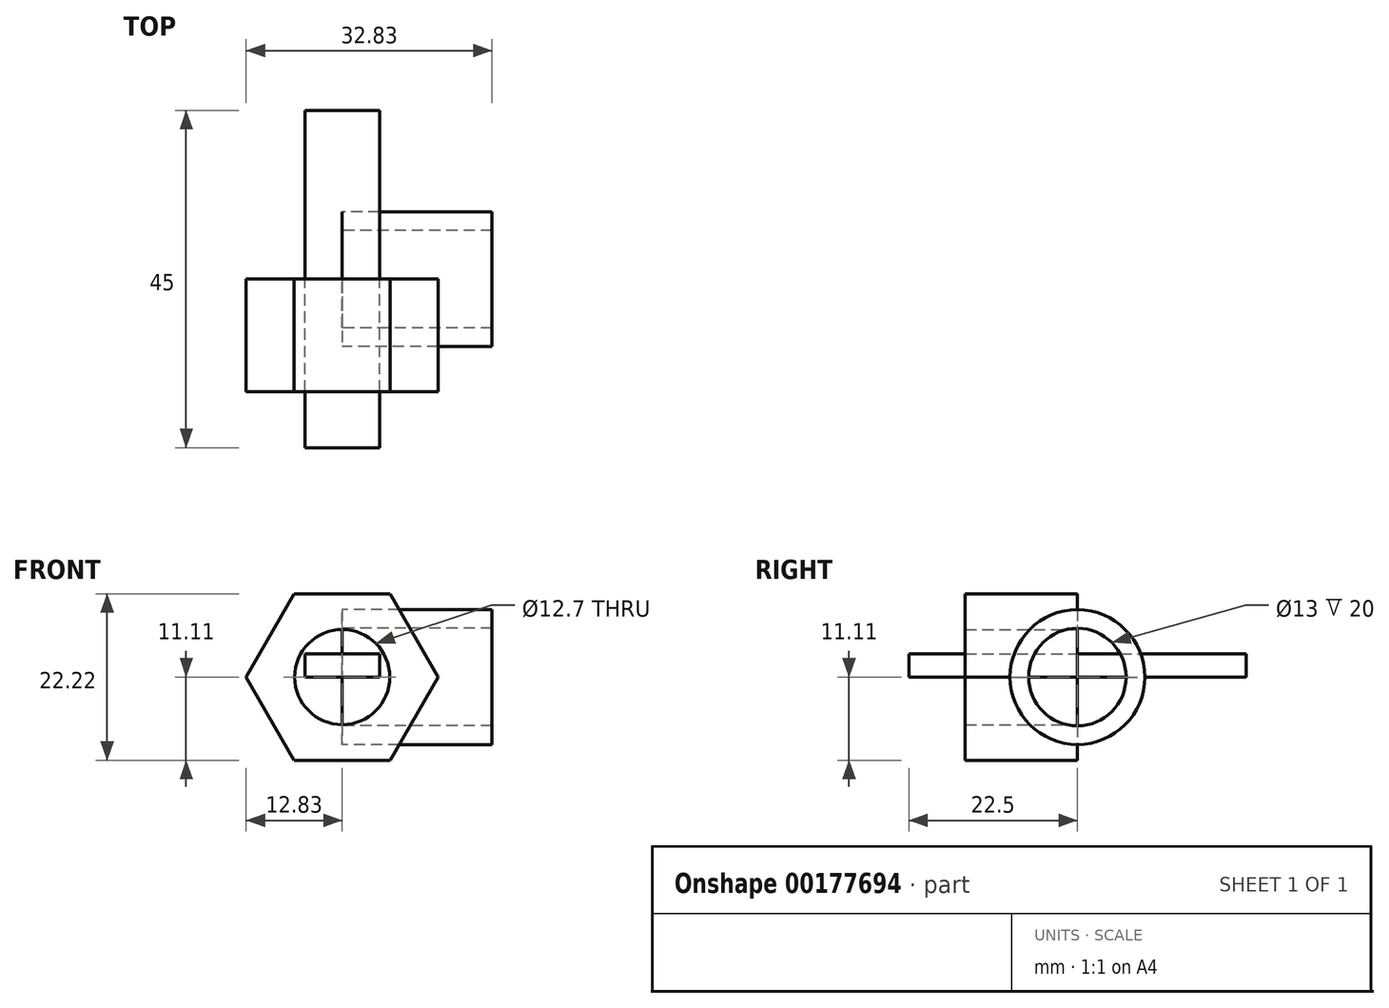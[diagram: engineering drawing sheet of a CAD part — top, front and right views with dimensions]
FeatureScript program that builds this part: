
annotation { "Feature Type Name" : "Feature", "Feature Type Description" : "" }
export const myFeature = defineFeature(function(context is Context, id is Id, definition is map)
    precondition{}
    {
        {
            var Q0;
            Q0=qCreatedBy(makeId("Front.planeOp"),FACE);
            var sketch = newSketch(context, id + "F0", { "sketchPlane" : qUnion([Q0])});
            skCircle(sketch, "E0.cCircle", {"center": v(0, 0) * mm, "radius": 11.11 * mm, "construction": true});
            skLineSegment(sketch, "E0.0", {"start": v(-6.42, 11.11) * mm, "end": v(6.42, 11.11) * mm});
            skLineSegment(sketch, "E0.1", {"start": v(6.42, 11.11) * mm, "end": v(12.83, 0) * mm});
            skLineSegment(sketch, "E0.2", {"start": v(12.83, 0) * mm, "end": v(6.42, -11.11) * mm});
            skLineSegment(sketch, "E0.3", {"start": v(6.42, -11.11) * mm, "end": v(-6.42, -11.11) * mm});
            skLineSegment(sketch, "E0.4", {"start": v(-6.42, -11.11) * mm, "end": v(-12.83, 0) * mm});
            skLineSegment(sketch, "E0.5", {"start": v(-12.83, 0) * mm, "end": v(-6.42, 11.11) * mm});
            skPoint(sketch, "E0.0.midPoint", {"position": v(0, 11.11) * mm});
            skCircle(sketch, "E1", {"center": v(0, 0) * mm, "radius": 6.35 * mm});
            skSolve(sketch);
        }
        {
            var Q0;
            Q0 = qSketchRegion(id + "F0", true);
            extrude(context, id + "F1", {"entities" : qUnion([Q0]), "depth" : 15 * mm});
        }
        {
            var Q0;
            Q0=qCreatedBy(makeId("Right.planeOp"),FACE);
            var sketch = newSketch(context, id + "F2", { "sketchPlane" : qUnion([Q0])});
            skCircle(sketch, "E2", {"center": v(0, 0) * mm, "radius": 6.5 * mm});
            skCircle(sketch, "E3", {"center": v(0, 0) * mm, "radius": 9 * mm});
            skSolve(sketch);
        }
        {
            var Q0;
            Q0 = qSketchRegion(id + "F2", true);
            extrude(context, id + "F3", {"entities" : qUnion([Q0]), "depth" : 20 * mm});
        }
        {
            var Q0;
            Q0=qCreatedBy(makeId("Top.planeOp"),FACE);
            var sketch = newSketch(context, id + "F4", { "sketchPlane" : qUnion([Q0])});
            skLineSegment(sketch, "E4.bottom", {"start": v(5, -22.5) * mm, "end": v(-5, -22.5) * mm});
            skLineSegment(sketch, "E4.top", {"start": v(5, 22.5) * mm, "end": v(-5, 22.5) * mm});
            skLineSegment(sketch, "E4.left", {"start": v(5, -22.5) * mm, "end": v(5, 22.5) * mm});
            skLineSegment(sketch, "E4.right", {"start": v(-5, -22.5) * mm, "end": v(-5, 22.5) * mm});
            skPoint(sketch, "E4.middle", {"position": v(0, 0) * mm});
            skSolve(sketch);
        }
        {
            var Q0;
            Q0 = qSketchRegion(id + "F4", true);
            extrude(context, id + "F5", {"entities" : qUnion([Q0]), "depth" : 3.12 * mm});
        }
    });
